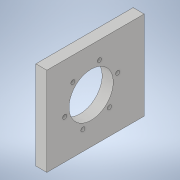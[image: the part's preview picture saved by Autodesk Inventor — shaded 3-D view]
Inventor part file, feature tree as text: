
AUTODESK INVENTOR PART (.ipt)
format: ipt  version: 2021 (Build 250183000, 183)  size: 128,000 bytes
history: native  units: in
note: dims shown in document units (in); Inventor stores cm internally (conversion verified against a paired STEP export)
features: other x3, sketch x3
ambient origin geometry x8: Origin, YZ Plane, XZ Plane, XY Plane, X Axis, Y Axis, Z Axis, Center Point
bodies: Solid1 (feature_tree)
feature tree (6):
  other  "motor mount.ipt"
  other  "Solid1::motor mount.ipt"
  other  "TaggingFeature1"
  sketch  "Sketch1"  dims[d0=0.3937in]
  sketch  "Sketch2"
  sketch  "Sketch3"
